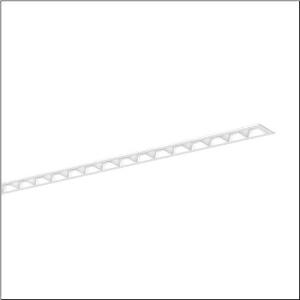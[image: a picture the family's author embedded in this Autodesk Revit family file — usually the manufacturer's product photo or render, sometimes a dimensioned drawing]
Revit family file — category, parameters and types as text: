
# Revit family: silica_21_51mx16dc4awb
name_source: partatom
category: Lighting Fixtures
units: mm (PartAtom-declared; Revit-internal decimal feet)

## family parameters
Cut with Voids When Loaded = No
Host = Face
Light Source = No
Part Type = Normal
Room Calculation Point = No
Round Connector Dimension = Use Diameter
Shared = No

## types (1)
- --- (1 x LED, 10800 lm, 60.6 W, 4000K)
    Apparent Load = 61 VA
    CIE Flux Codes = 83 98 100 100 100
    Color Rendering = 80
    Color Temperature = 4000K
    Default Elevation = 1800 mm
    Description = Silica 21, office luminaire, primary light control with darklight reflector, of PMMA, white, CAT 2 (L<= 3000cd/m²), light emission: direct distribution, primary light characteristic: symmetric, installation type: recessed, LED, rated luminous flux: 10.800lm, luminous efficacy: 178lm/W, light colour: 840, colour temperature: 4000K, control gear: DALI 2, with terminal, 3+2-pole, max. 2.5mm², mains connection: 220..240V, AC, 50/60Hz, rated input power: 60.6W, luminaire housing, of aluminium, traffic white (RAL 9016), length: 3.028mm, width: 79mm, height: 53mm, protection rating (complete): IP20, insulation class (complete): insulation class I (protective earthing), certification: CE, ENEC, VDE, permissible operating ambient temperature: 0..+35°C, standard: EN 50419, packaging unit: 1 piece
    Height = 0 mm  [stored 0 ft]
    Lamp = 1 x LED
    Lamp Light Flux = 10800 lm
    Lamp Power = 60.6 W
    Lamp count = 1
    Length = 3027 mm
    Luminous efficacy = 178 lm/W
    Manufacturer = Siteco
    ModVariant = No
    Model = 51MX16DC4AWB
    Mounting Place = Ceiling
    Mounting Type = Recessed
    Number of Poles = 1
    OnlyDefault = Yes
    Power Factor = 1
    Product Name = Silica 21
    Product group = office luminaire | ceiling recessed
    ProductGroupID = 400
    Protection Class = Protection class I
    Protection Degree = IP 20
    RLX_Detail_Level = 1
    RLX_Emergency_Light_Flux = 0 lm
    RLX_Emergency_Type = 0
    RLX_Emergency_Type_DB = No
    RlxData = <blob elided: 60165 chars, md5=00665837>
    Socket = socket
    Standby Power = 0 W
    System Light Flux = 10800 lm
    System Power = 61 W
    Type Comments = factory setting: luminous flux: 100 % | dim-lin: 254 | 336 mA
    Type Image = l_1335884.jpg
    URL = http://relux.com
    VarID = @adj_125765
    Voltage = 0 V
    Weight = 0.00 kg
    Width = 79 mm

note: [stored X ft] marks values corroborated as IEEE doubles in the binary element streams (Revit-internal decimal feet)

## geometry (parser evidence)
native form markers: Blend x4, Sweep x10
no freeform markers — native parametric forms only
